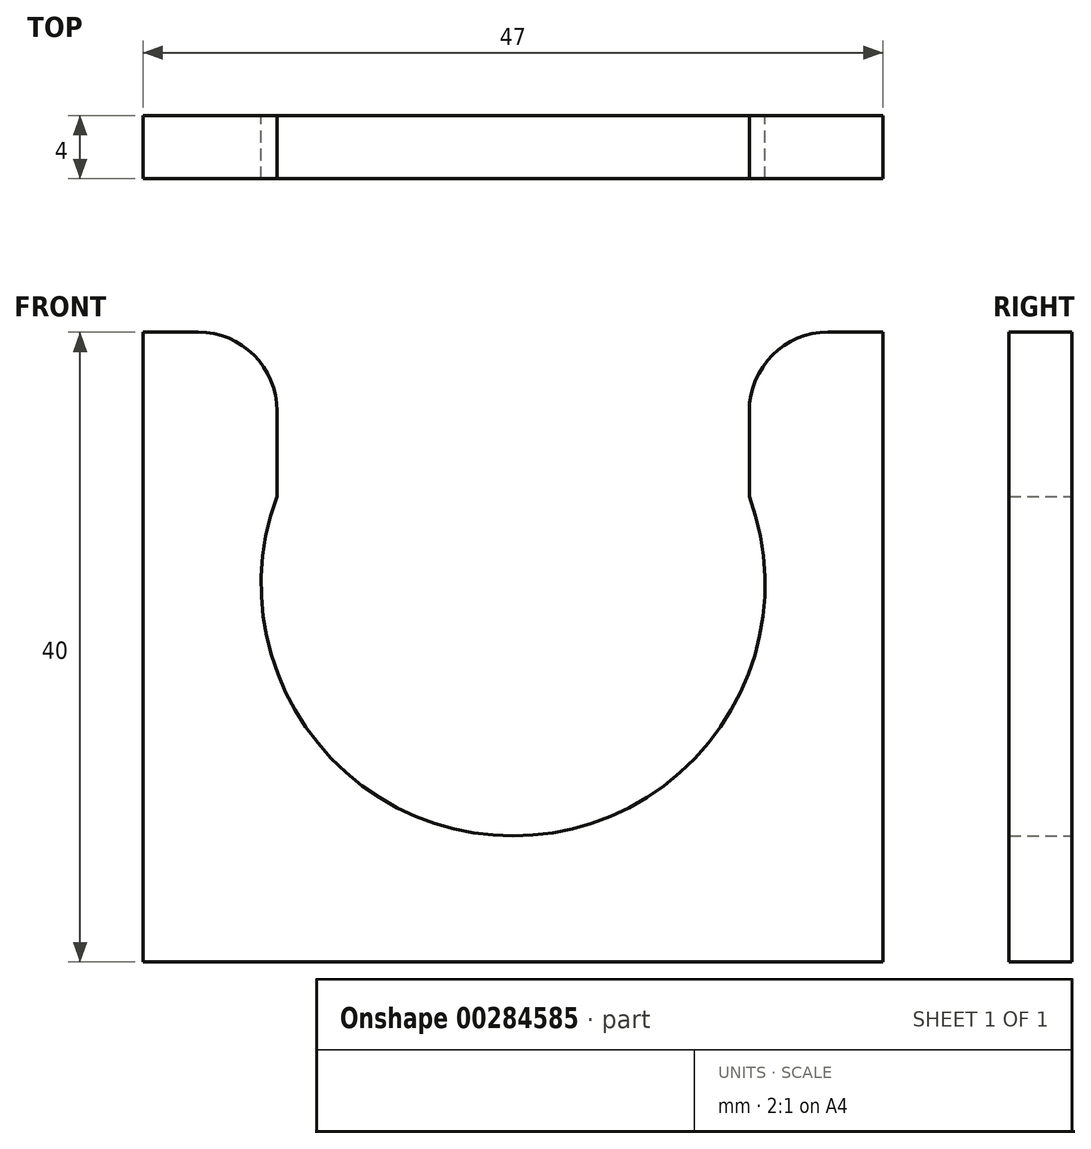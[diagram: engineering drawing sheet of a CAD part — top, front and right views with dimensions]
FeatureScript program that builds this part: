
annotation { "Feature Type Name" : "Feature", "Feature Type Description" : "" }
export const myFeature = defineFeature(function(context is Context, id is Id, definition is map)
    precondition{}
    {
        {
            var Q0;
            Q0=qCreatedBy(makeId("Front.planeOp"),FACE);
            var sketch = newSketch(context, id + "F0", { "sketchPlane" : qUnion([Q0])});
            skLineSegment(sketch, "E0.bottom", {"start": v(-20, 20) * mm, "end": v(-23.5, 20) * mm});
            skLineSegment(sketch, "E0.top", {"start": v(23.5, -20) * mm, "end": v(-23.5, -20) * mm});
            skLineSegment(sketch, "E0.left", {"start": v(23.5, 20) * mm, "end": v(23.5, -20) * mm});
            skLineSegment(sketch, "E0.right", {"start": v(-23.5, 20) * mm, "end": v(-23.5, -20) * mm});
            skPoint(sketch, "E0.middle", {"position": v(0, 0) * mm});
            skLineSegment(sketch, "E1", {"start": v(0, -20) * mm, "end": v(0, -12) * mm});
            skPoint(sketch, "E1.endSnap0", {"position": v(0, -20) * mm});
            skPoint(sketch, "E2", {"position": v(0, 4) * mm});
            skArc(sketch, "E3", {"start": v(-15, 9.57) * mm, "mid": v(0, -12) * mm, "end": v(15, 9.57) * mm});
            skLineSegment(sketch, "E4", {"start": v(0, 20) * mm, "end": v(15, 20) * mm});
            skLineSegment(sketch, "E5", {"start": v(15, 20) * mm, "end": v(-15, 20) * mm});
            skLineSegment(sketch, "E6", {"start": v(-15, 15) * mm, "end": v(-15, 9.5) * mm});
            skLineSegment(sketch, "E7", {"start": v(15, 9.5) * mm, "end": v(15, 15) * mm});
            skPoint(sketch, "E8.newPointA", {"position": v(23.5, 20) * mm});
            skPoint(sketch, "E8.newPointB", {"position": v(-15, 20) * mm});
            skArc(sketch, "E8.filletArc", {"start": v(-15, 15) * mm, "mid": v(-16.46, 18.54) * mm, "end": v(-20, 20) * mm});
            skLineSegment(sketch, "E9", {"start": v(20, 20) * mm, "end": v(23.5, 20) * mm});
            skPoint(sketch, "E10.visualSharp", {"position": v(15, 20) * mm});
            skArc(sketch, "E10.filletArc", {"start": v(20, 20) * mm, "mid": v(16.46, 18.54) * mm, "end": v(15, 15) * mm});
            skSolve(sketch);
        }
        {
            var Q0;
            Q0=qSketchRegion(id+"F0",true);
            extrude(context, id + "F1", {"entities" : qUnion([Q0]), "depth" : 4 * mm});
        }
    });
